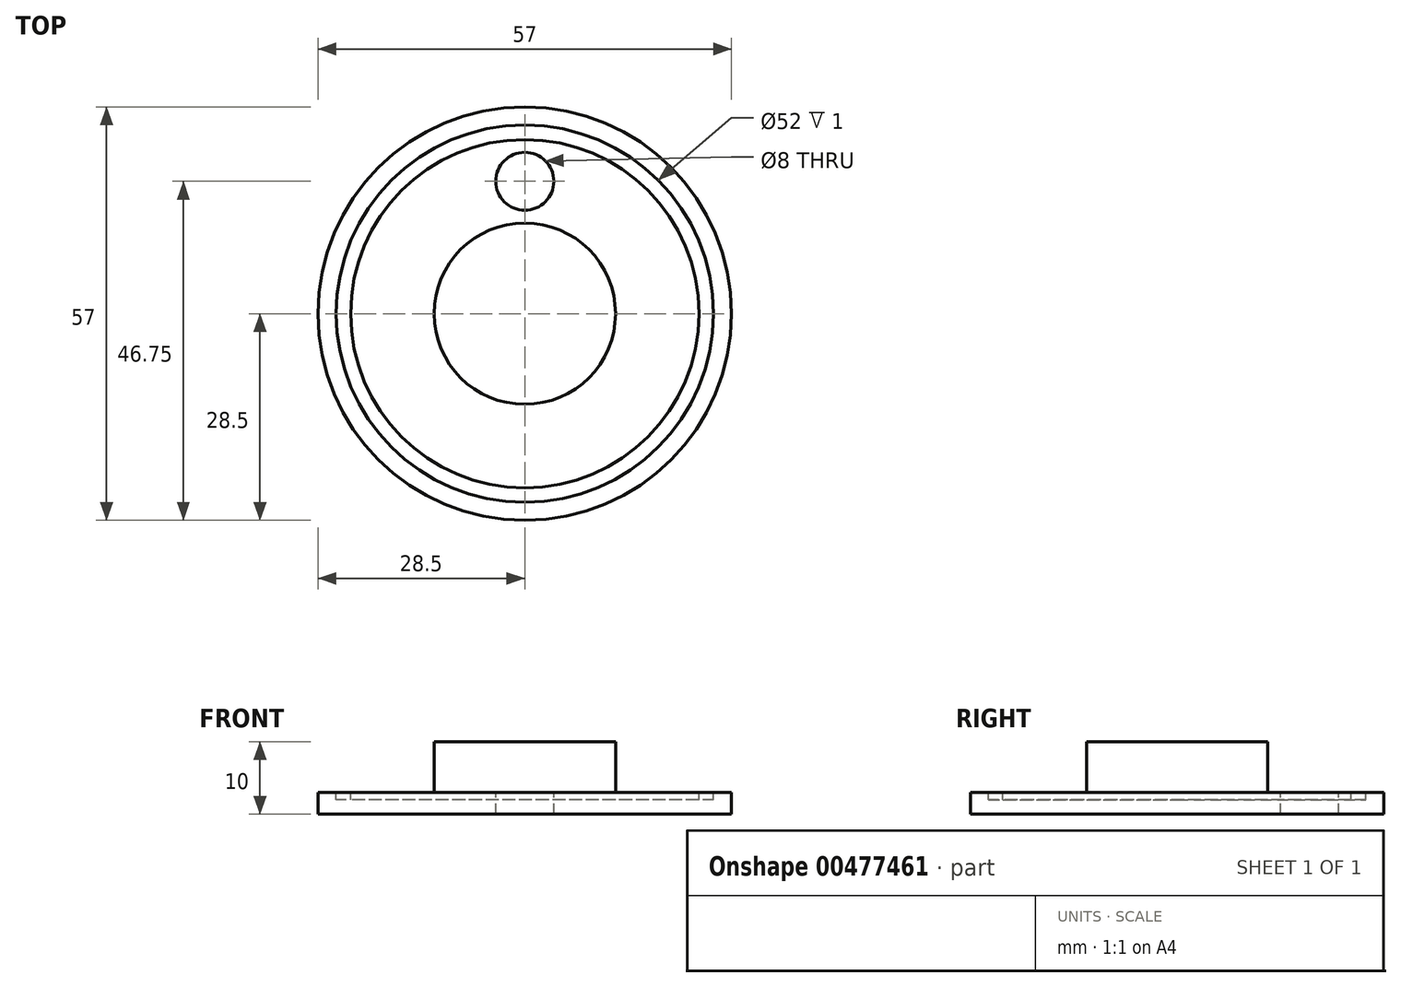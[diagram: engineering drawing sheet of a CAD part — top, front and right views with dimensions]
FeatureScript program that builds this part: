
annotation { "Feature Type Name" : "Feature", "Feature Type Description" : "" }
export const myFeature = defineFeature(function(context is Context, id is Id, definition is map)
    precondition{}
    {
        {
            var Q0;
            Q0=qCreatedBy(makeId("Top.planeOp"),FACE);
            var sketch = newSketch(context, id + "F0", { "sketchPlane" : qUnion([Q0])});
            skCircle(sketch, "E0", {"center": v(0, 0) * mm, "radius": 28.5 * mm});
            skSolve(sketch);
        }
        {
            var Q0;
            Q0=qSketchRegion(id+"F0",true);
            extrude(context, id + "F1", {"entities" : qUnion([Q0]), "depth" : 3 * mm});
        }
        {
            var Q0;
            Q0=makeQuery(id+"F1.opExtrude","CAP_FACE",FACE,{"disambiguationData":[OSD([sQuery(id+"F0.wireOp",EDGE,"E0")])],"isStart":false});
            var sketch = newSketch(context, id + "F2", { "sketchPlane" : qUnion([Q0])});
            skCircle(sketch, "E1", {"center": v(0, 0) * mm, "radius": 26 * mm});
            skCircle(sketch, "E2", {"center": v(0, 0) * mm, "radius": 24 * mm});
            skSolve(sketch);
        }
        {
            var Q0;
            Q0=qSketchRegion(id+"F2",true);
            extrude(context, id + "F3", {"entities" : qUnion([Q0]), "operationType" : NewBodyOperationType.REMOVE, "oppositeDirection" : true, "depth" : 1 * mm});
        }
        {
            var Q0;
            Q0=makeQuery(id+"F3.boolean.opBoolean","SPLIT",FACE,{"disambiguationData":[TD([makeQuery(id+"F3.opExtrude","SWEPT_FACE",FACE,{"disambiguationData":[OSD([sQuery(id+"F2.wireOp",EDGE,"E2")])]})])],"derivedFrom":makeQuery(id+"F1.opExtrude","CAP_FACE",FACE,{"disambiguationData":[OSD([sQuery(id+"F0.wireOp",EDGE,"E0")])],"isStart":false})});
            var sketch = newSketch(context, id + "F4", { "sketchPlane" : qUnion([Q0])});
            skCircle(sketch, "E3", {"center": v(0, 0) * mm, "radius": 12.5 * mm});
            skSolve(sketch);
        }
        {
            var Q0;
            Q0 = qSketchRegion(id + "F4", true);
            extrude(context, id + "F5", {"entities" : qUnion([Q0]), "operationType" : NewBodyOperationType.ADD, "depth" : 7 * mm});
        }
        {
            var Q0;
            Q0=makeQuery(id+"F3.boolean.opBoolean","SPLIT",FACE,{"disambiguationData":[TD([makeQuery(id+"F3.opExtrude","SWEPT_FACE",FACE,{"disambiguationData":[OSD([sQuery(id+"F2.wireOp",EDGE,"E2")])]})])],"derivedFrom":makeQuery(id+"F1.opExtrude","CAP_FACE",FACE,{"disambiguationData":[OSD([sQuery(id+"F0.wireOp",EDGE,"E0")])],"isStart":false})});
            var sketch = newSketch(context, id + "F6", { "sketchPlane" : qUnion([Q0])});
            skCircle(sketch, "E4", {"center": v(0, 18.25) * mm, "radius": 4 * mm});
            skSolve(sketch);
        }
        {
            var Q0;
            Q0 = qSketchRegion(id + "F6", true);
            extrude(context, id + "F7", {"entities" : qUnion([Q0]), "operationType" : NewBodyOperationType.REMOVE, "oppositeDirection" : true, "depth" : 3 * mm});
        }
    });
